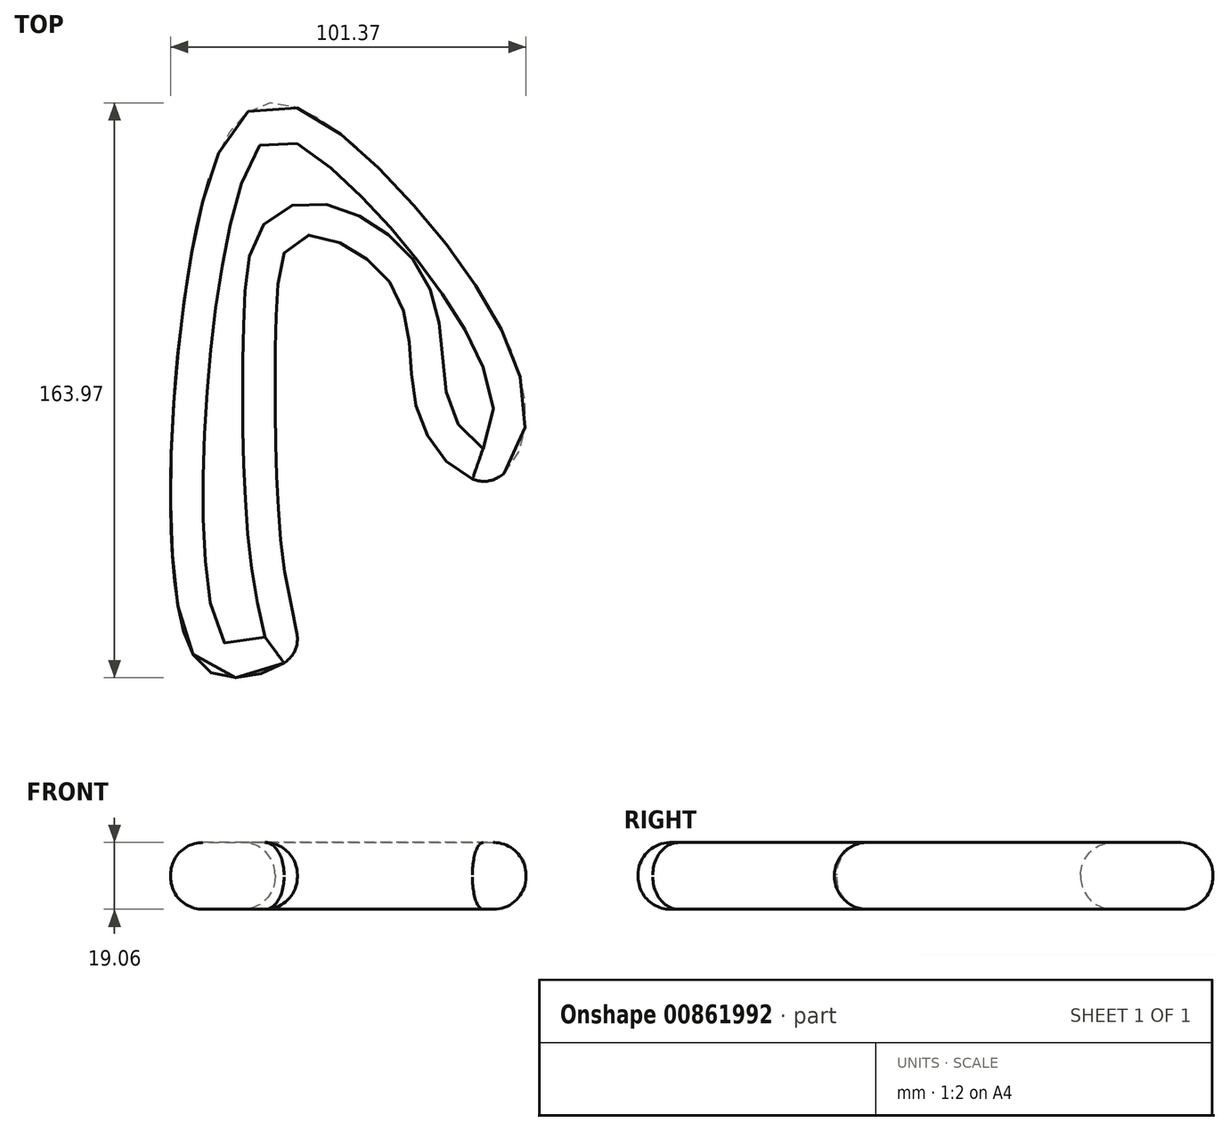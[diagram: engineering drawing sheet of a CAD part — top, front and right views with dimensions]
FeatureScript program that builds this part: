
annotation { "Feature Type Name" : "Feature", "Feature Type Description" : "" }
export const myFeature = defineFeature(function(context is Context, id is Id, definition is map)
    precondition{}
    {
        {
            var Q0;
            Q0=qCreatedBy(makeId("Top.planeOp"),FACE);
            var sketch = newSketch(context, id + "F0", { "sketchPlane" : qUnion([Q0])});
            skLineSegment(sketch, "E0", {"start": v(-51.7, -50.28) * mm, "end": v(-51.7, 51.32) * mm});
            skLineSegment(sketch, "E1", {"start": v(-51.7, 51.32) * mm, "end": v(-41.03, 51.32) * mm});
            skLineSegment(sketch, "E2", {"start": v(-41.03, 51.32) * mm, "end": v(-41.03, -50.28) * mm});
            skLineSegment(sketch, "E3", {"start": v(-41.03, -50.28) * mm, "end": v(-51.7, -50.28) * mm});
            skFitSpline(sketch, "E4", {"points": [v(-56.83, 61.26) * mm, v(-59.56, -52.95) * mm, v(-46.25, -64.69) * mm, v(-28.88, -58.06) * mm, v(-30.58, -38.29) * mm, v(-33.65, 37.4) * mm, v(-26.5, 61.26) * mm, v(0, 46.26) * mm, v(7.26, 9.44) * mm, v(26.35, -8.63) * mm, v(37.6, 11.15) * mm, v(2.49, 73.54) * mm, v(-36.38, 99.1) * mm, v(-56.83, 61.26) * mm]});
            skSolve(sketch);
        }
        {
            var Q0;
            Q0=makeQuery(id+"F0.imprint","IMPRINT",FACE,{"disambiguationData":[TD([[makeQuery(id+"F0.imprint","IMPRINT",EDGE,{"derivedFrom":sQuery(id+"F0.wireOp",EDGE,"E0")}),1.0]])]});
            var Q1;
            Q1=makeQuery(id+"F0.imprint","IMPRINT",FACE,{"disambiguationData":[TD([[makeQuery(id+"F0.imprint","IMPRINT",EDGE,{"derivedFrom":sQuery(id+"F0.wireOp",EDGE,"E0")}),-1.0]])]});
            extrude(context, id + "F1", {"entities" : qUnion([Q0, Q1]), "endBound" : BoundingType.SYMMETRIC, "depth" : 19.05 * mm, "offsetDistance" : 25.4 * mm});
        }
        {
            var Q0;
            Q0=makeQuery(id+"F1.opExtrude","CAP_FACE",FACE,{"disambiguationData":[OSD([sQuery(id+"F0.wireOp",EDGE,"E4")])],"isStart":false});
            fillet(context, id + "F2", {"entities" : qUnion([Q0]), "radius" : 9.22 * mm, "tangentPropagation" : true, "allowEdgeOverflow" : false});
        }
        {
            var Q0;
            Q0=makeQuery(id+"F1.opExtrude","CAP_FACE",FACE,{"disambiguationData":[OSD([sQuery(id+"F0.wireOp",EDGE,"E4")])],"isStart":true});
            fillet(context, id + "F3", {"entities" : qUnion([Q0]), "radius" : 9.22 * mm, "tangentPropagation" : true, "allowEdgeOverflow" : false});
        }
    });
